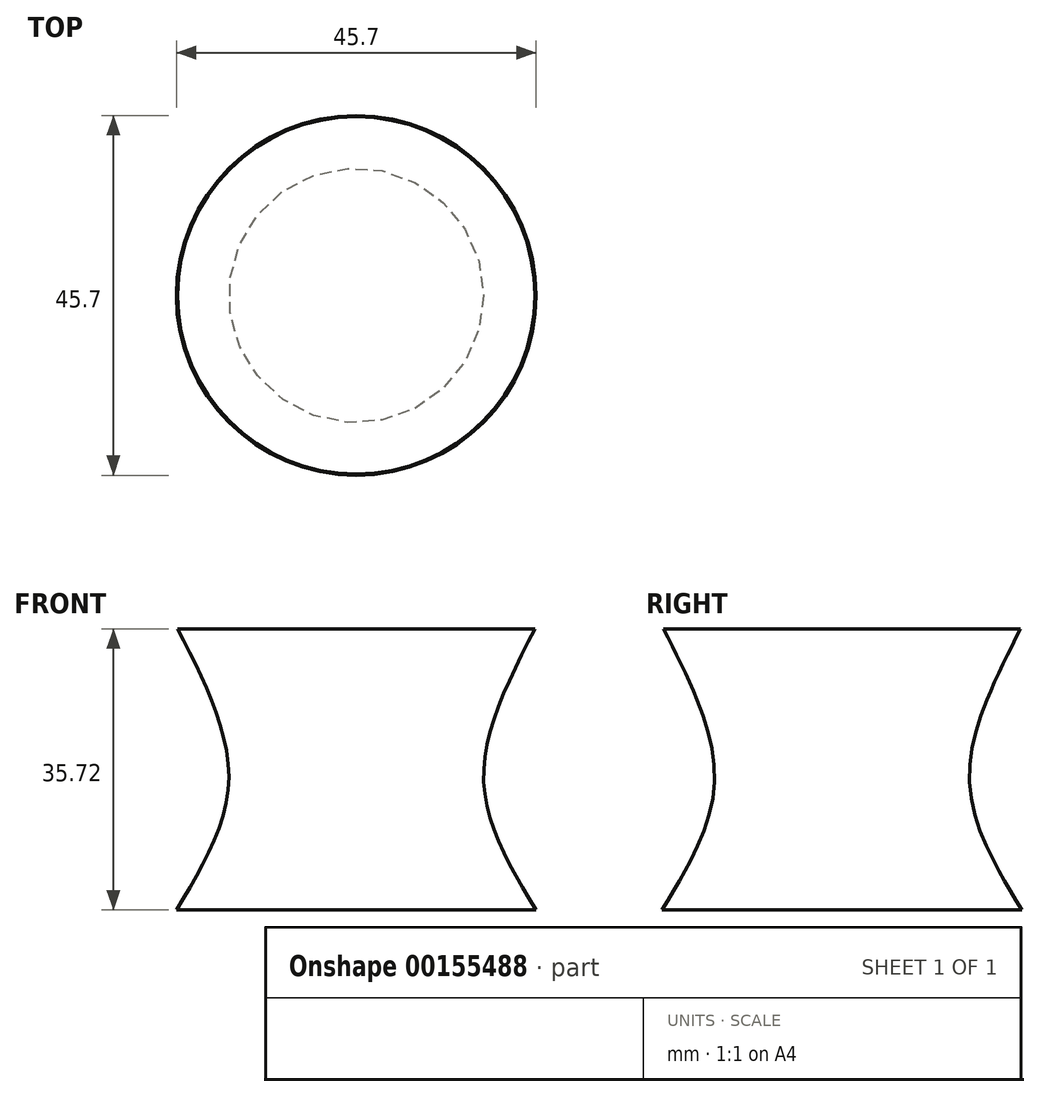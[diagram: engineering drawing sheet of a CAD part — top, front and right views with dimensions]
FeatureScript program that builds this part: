
annotation { "Feature Type Name" : "Feature", "Feature Type Description" : "" }
export const myFeature = defineFeature(function(context is Context, id is Id, definition is map)
    precondition{}
    {
        {
            var Q0;
            Q0=qCreatedBy(makeId("Front.planeOp"),FACE);
            var sketch = newSketch(context, id + "F0", { "sketchPlane" : qUnion([Q0])});
            skLineSegment(sketch, "E0", {"start": v(0, 0) * mm, "end": v(22.85, 0) * mm});
            skLineSegment(sketch, "E1", {"start": v(22.69, 35.72) * mm, "end": v(0, 35.72) * mm});
            skLineSegment(sketch, "E2", {"start": v(0, 35.72) * mm, "end": v(-22.67, 35.72) * mm});
            skLineSegment(sketch, "E3", {"start": v(0, 0) * mm, "end": v(-22.85, 0) * mm});
            skLineSegment(sketch, "E4", {"start": v(0, 35.72) * mm, "end": v(0, 0) * mm});
            skFitSpline(sketch, "E5", {"points": [v(-22.85, 0) * mm, v(-16.2, 16.47) * mm, v(-22.67, 35.72) * mm], "startDerivative": vector(20.15, 33.31) * mm, "endDerivative": vector(-19.34, 38.07) * mm});
            skFitSpline(sketch, "E6", {"points": [v(22.69, 35.72) * mm, v(16.18, 16.47) * mm, v(22.85, 0) * mm], "startDerivative": vector(-19.4, -38.07) * mm, "endDerivative": vector(20.17, -33.32) * mm});
            skSolve(sketch);
        }
        {
            var Q0;
            Q0=makeQuery(id+"F0.imprint","IMPRINT",FACE,{"disambiguationData":[TD([[makeQuery(id+"F0.imprint","IMPRINT",EDGE,{"derivedFrom":sQuery(id+"F0.wireOp",EDGE,"E0")}),1.0]])]});
            var Q1;
            Q1=sQuery(id+"F0.wireOp",EDGE,"E4");
            revolve(context, id + "F1", {"entities" : qUnion([Q0]), "axis" : qUnion([Q1]), "revolveType" : RevolveType.FULL});
        }
    });
